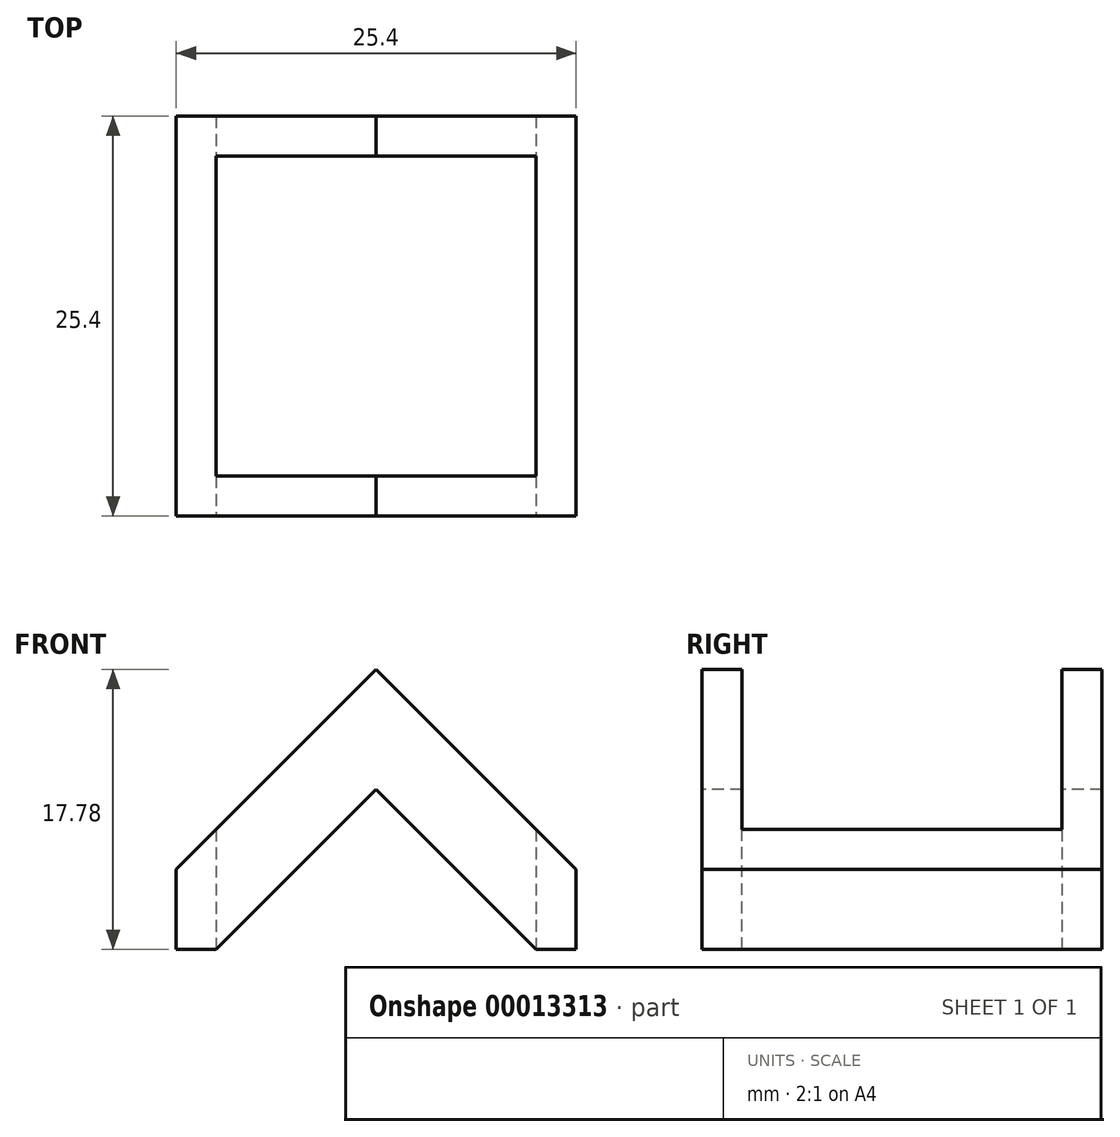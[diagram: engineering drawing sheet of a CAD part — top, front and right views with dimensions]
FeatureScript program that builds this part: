
annotation { "Feature Type Name" : "Feature", "Feature Type Description" : "" }
export const myFeature = defineFeature(function(context is Context, id is Id, definition is map)
    precondition{}
    {
        {
            var Q0;
            Q0=qCreatedBy(makeId("Top.planeOp"),FACE);
            var sketch = newSketch(context, id + "F0", { "sketchPlane" : qUnion([Q0])});
            skLineSegment(sketch, "E0.bottom", {"start": v(-12.7, -12.7) * mm, "end": v(12.7, -12.7) * mm});
            skLineSegment(sketch, "E0.top", {"start": v(-12.7, 12.7) * mm, "end": v(12.7, 12.7) * mm});
            skLineSegment(sketch, "E0.left", {"start": v(-12.7, -12.7) * mm, "end": v(-12.7, 12.7) * mm});
            skLineSegment(sketch, "E0.right", {"start": v(12.7, -12.7) * mm, "end": v(12.7, 12.7) * mm});
            skLineSegment(sketch, "E1.bottom", {"start": v(-10.16, -10.16) * mm, "end": v(10.16, -10.16) * mm});
            skLineSegment(sketch, "E1.top", {"start": v(-10.16, 10.16) * mm, "end": v(10.16, 10.16) * mm});
            skLineSegment(sketch, "E1.left", {"start": v(-10.16, -10.16) * mm, "end": v(-10.16, 10.16) * mm});
            skLineSegment(sketch, "E1.right", {"start": v(10.16, -10.16) * mm, "end": v(10.16, 10.16) * mm});
            skSolve(sketch);
        }
        {
            var Q0;
            Q0=makeQuery(id+"F0.imprint","IMPRINT",FACE,{"disambiguationData":[TD([[makeQuery(id+"F0.imprint","IMPRINT",EDGE,{"derivedFrom":sQuery(id+"F0.wireOp",EDGE,"E0.bottom")}),1.0]])]});
            extrude(context, id + "F1", {"entities" : qUnion([Q0]), "depth" : 5.08 * mm});
        }
        {
            var Q0;
            Q0=makeQuery(id+"F1.opExtrude","SWEPT_FACE",FACE,{"disambiguationData":[OSD([sQuery(id+"F0.wireOp",EDGE,"E0.bottom")])]});
            var sketch = newSketch(context, id + "F2", { "sketchPlane" : qUnion([Q0])});
            skLineSegment(sketch, "E2", {"start": v(-10.16, 0) * mm, "end": v(0, 10.16) * mm});
            skLineSegment(sketch, "E3", {"start": v(10.16, 0) * mm, "end": v(0, 10.16) * mm});
            skLineSegment(sketch, "E4", {"start": v(-12.7, 5.08) * mm, "end": v(0, 17.78) * mm});
            skLineSegment(sketch, "E5", {"start": v(12.7, 5.08) * mm, "end": v(0, 17.78) * mm});
            skPoint(sketch, "E6.start.orphan", {"position": v(0, 0) * mm});
            skLineSegment(sketch, "E7", {"start": v(-12.7, 5.08) * mm, "end": v(-12.7, 0) * mm});
            skLineSegment(sketch, "E8", {"start": v(-12.7, 0) * mm, "end": v(-10.16, 0) * mm});
            skLineSegment(sketch, "E9", {"start": v(10.16, 0) * mm, "end": v(12.7, 0) * mm});
            skLineSegment(sketch, "E10", {"start": v(12.7, 0) * mm, "end": v(12.7, 5.08) * mm});
            skSolve(sketch);
        }
        {
            var Q0;
            {var subQ6=sQuery(id+"F2.wireOp",EDGE,"E4");Q0=makeQuery(id+"F2.imprint","IMPRINT",FACE,{"disambiguationData":[TD([[makeQuery(id+"F2.imprint","IMPRINT",EDGE,{"derivedFrom":subQ6}),-1.0]])]});}
            extrude(context, id + "F3", {"entities" : qUnion([Q0]), "operationType" : NewBodyOperationType.ADD, "oppositeDirection" : true, "depth" : 25.4 * mm});
        }
        {
            var Q0;
            Q0=makeQuery(id+"F1.opExtrude","CAP_FACE",FACE,{"disambiguationData":[OSD([sQuery(id+"F0.wireOp",EDGE,"E0.bottom"),sQuery(id+"F0.wireOp",EDGE,"E0.top"),sQuery(id+"F0.wireOp",EDGE,"E0.left"),sQuery(id+"F0.wireOp",EDGE,"E0.right"),sQuery(id+"F0.wireOp",EDGE,"E1.bottom"),sQuery(id+"F0.wireOp",EDGE,"E1.top"),sQuery(id+"F0.wireOp",EDGE,"E1.left"),sQuery(id+"F0.wireOp",EDGE,"E1.right")])],"isStart":true});
            var sketch = newSketch(context, id + "F4", { "sketchPlane" : qUnion([Q0])});
            skSolve(sketch);
        }
        {
            var Q0;
            Q0 = qSketchRegion(id + "F4", true);
            var Q1;
            Q1=makeQuery(id+"F4.imprint","IMPRINT",FACE,{"disambiguationData":[TD([[makeQuery(id+"F4.imprint","IMPRINT",EDGE,{"derivedFrom":makeQuery(id+"F1.opExtrude","CAP_EDGE",EDGE,{"disambiguationData":[OSD([sQuery(id+"F0.wireOp",EDGE,"E1.bottom")])],"isStart":true})}),-1.0]])]});
            extrude(context, id + "F5", {"entities" : qUnion([Q0, Q1]), "operationType" : NewBodyOperationType.REMOVE, "oppositeDirection" : true, "depth" : 25.4 * mm});
        }
        {
            var Q0;
            {var subQ0=sQuery(id+"F0.wireOp",EDGE,"E0.bottom");Q0=makeQuery(id+"F3.boolean.opBoolean","MERGE",FACE,{"derivedFrom":[makeQuery(id+"F1.opExtrude","SWEPT_FACE",FACE,{"disambiguationData":[OSD([subQ0])]}),makeQuery(id+"F3.opExtrude","CAP_FACE",FACE,{"disambiguationData":[OSD([subQ0,sQuery(id+"F2.wireOp",EDGE,"E2"),sQuery(id+"F2.wireOp",EDGE,"E3"),sQuery(id+"F2.wireOp",EDGE,"E4"),sQuery(id+"F2.wireOp",EDGE,"E5")])],"isStart":true})]});}
            var sketch = newSketch(context, id + "F6", { "sketchPlane" : qUnion([Q0])});
            skLineSegment(sketch, "E11", {"start": v(-5.08, 5.08) * mm, "end": v(-12.76, -2.6) * mm});
            skLineSegment(sketch, "E12", {"start": v(5.08, 5.08) * mm, "end": v(12.19, -2.03) * mm});
            skSolve(sketch);
        }
        {
            var Q0;
            {var subQ0=sQuery(id+"F0.wireOp",EDGE,"E0.bottom");var subQ6=makeQuery(id+"F1.opExtrude","CAP_EDGE",EDGE,{"disambiguationData":[OSD([subQ0])],"isStart":false});Q0=makeQuery(id+"F6.imprint","IMPRINT",FACE,{"disambiguationData":[TD([[makeQuery(id+"F6.imprint","IMPRINT",EDGE,{"derivedFrom":subQ6}),-1.0]])]});}
            extrude(context, id + "F7", {"entities" : qUnion([Q0]), "operationType" : NewBodyOperationType.REMOVE, "oppositeDirection" : true, "depth" : 25.4 * mm});
        }
    });
